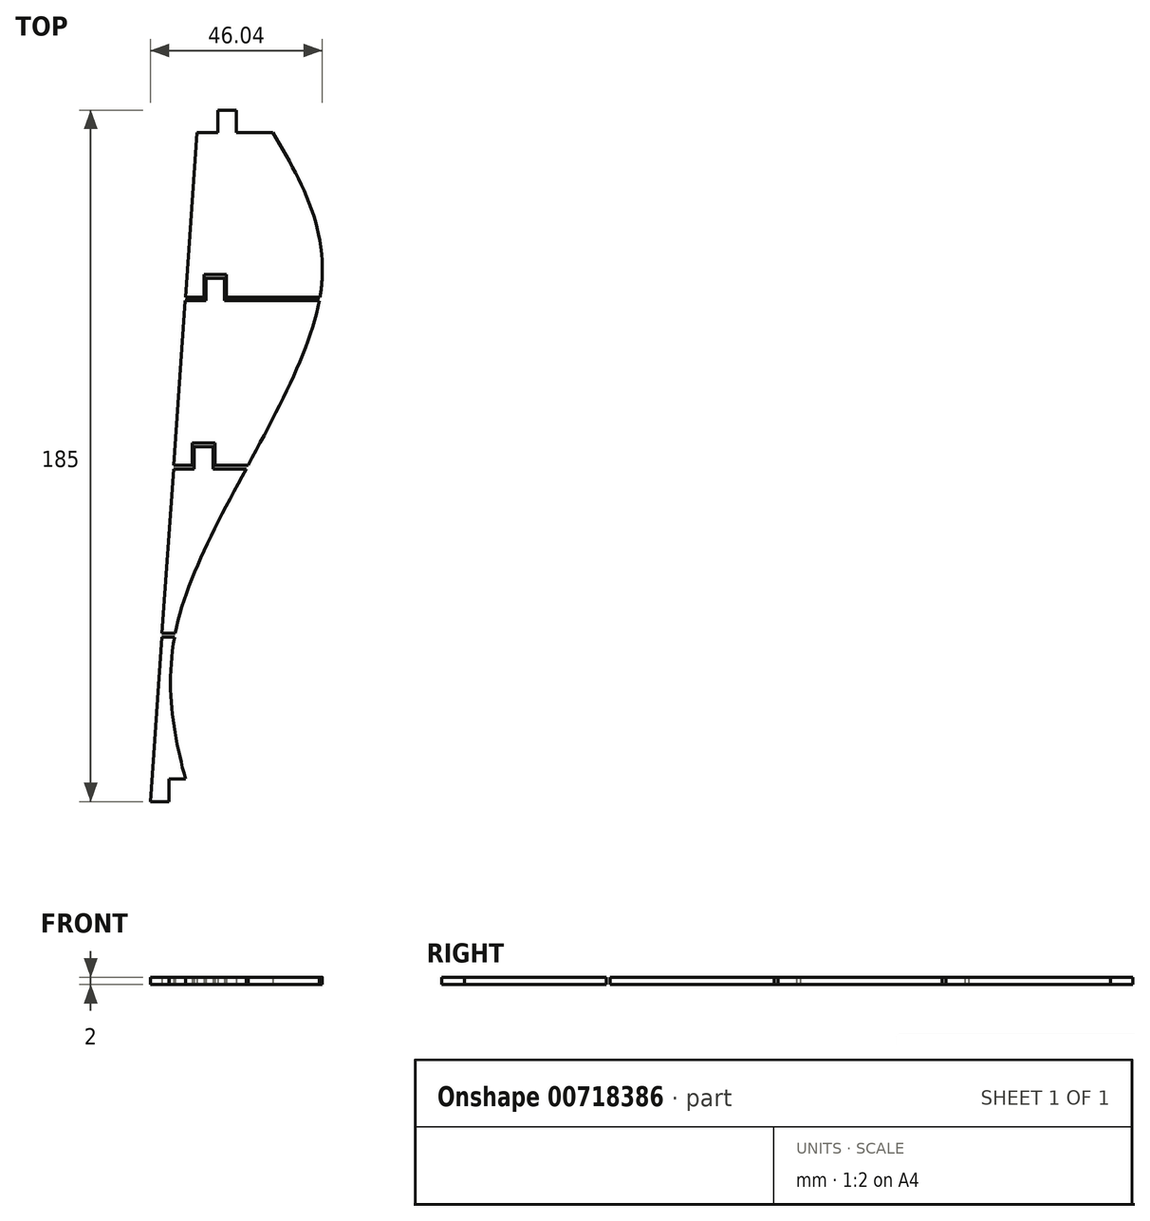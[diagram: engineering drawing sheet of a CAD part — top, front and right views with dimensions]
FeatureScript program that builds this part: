
annotation { "Feature Type Name" : "Feature", "Feature Type Description" : "" }
export const myFeature = defineFeature(function(context is Context, id is Id, definition is map)
    precondition{}
    {
        {
            var Q0;
            Q0=qCreatedBy(makeId("Top.planeOp"),FACE);
            var sketch = newSketch(context, id + "F0", { "sketchPlane" : qUnion([Q0])});
            skLineSegment(sketch, "E0", {"start": v(-23.52, 43.1) * mm, "end": v(-18.52, 43.1) * mm});
            skLineSegment(sketch, "E1", {"start": v(-26.65, -1.9) * mm, "end": v(-21.65, -1.9) * mm});
            skLineSegment(sketch, "E2", {"start": v(-29.78, -46.9) * mm, "end": v(-26.24, -46.9) * mm});
            skLineSegment(sketch, "E3", {"start": v(-32.9, -91.9) * mm, "end": v(-27.9, -91.9) * mm});
            skLineSegment(sketch, "E4.top", {"start": v(-18.52, 49.1) * mm, "end": v(-12.52, 49.1) * mm});
            skLineSegment(sketch, "E4.left", {"start": v(-18.52, 43.1) * mm, "end": v(-18.52, 49.1) * mm});
            skLineSegment(sketch, "E4.right", {"start": v(-12.52, 43.1) * mm, "end": v(-12.52, 49.1) * mm});
            skLineSegment(sketch, "E5.top", {"start": v(-21.65, 4.1) * mm, "end": v(-15.65, 4.1) * mm});
            skLineSegment(sketch, "E5.left", {"start": v(-21.65, -1.9) * mm, "end": v(-21.65, 4.1) * mm});
            skLineSegment(sketch, "E5.right", {"start": v(-15.65, -1.9) * mm, "end": v(-15.65, 4.1) * mm});
            skLineSegment(sketch, "E6.top", {"start": v(-27.9, -85.9) * mm, "end": v(-23.51, -85.9) * mm});
            skLineSegment(sketch, "E6.left", {"start": v(-27.9, -91.9) * mm, "end": v(-27.9, -85.9) * mm});
            skLineSegment(sketch, "E7.MirrorCS", {"start": v(12.52, 43.1) * mm, "end": v(12.52, 49.1) * mm});
            skLineSegment(sketch, "E8.MirrorCS", {"start": v(13.12, 49.1) * mm, "end": v(12.52, 49.1) * mm});
            skLineSegment(sketch, "E9", {"start": v(-20.46, 87.1) * mm, "end": v(-14.89, 87.1) * mm});
            skLineSegment(sketch, "E10", {"start": v(-23.59, 42.1) * mm, "end": v(-18.02, 42.1) * mm});
            skLineSegment(sketch, "E11", {"start": v(-26.72, -2.9) * mm, "end": v(-21.15, -2.9) * mm});
            skLineSegment(sketch, "E12", {"start": v(-29.84, -47.9) * mm, "end": v(-26.43, -47.9) * mm});
            skLineSegment(sketch, "E13.top", {"start": v(-14.89, 93.1) * mm, "end": v(-9.89, 93.1) * mm});
            skLineSegment(sketch, "E13.left", {"start": v(-14.89, 87.1) * mm, "end": v(-14.89, 93.1) * mm});
            skLineSegment(sketch, "E13.right", {"start": v(-9.89, 87.1) * mm, "end": v(-9.89, 93.1) * mm});
            skLineSegment(sketch, "E14.top", {"start": v(-18.02, 48.1) * mm, "end": v(-13.02, 48.1) * mm});
            skLineSegment(sketch, "E14.left", {"start": v(-18.02, 42.1) * mm, "end": v(-18.02, 48.1) * mm});
            skLineSegment(sketch, "E14.right", {"start": v(-13.02, 42.1) * mm, "end": v(-13.02, 48.1) * mm});
            skLineSegment(sketch, "E15.top", {"start": v(-21.15, 3.1) * mm, "end": v(-16.15, 3.1) * mm});
            skLineSegment(sketch, "E15.left", {"start": v(-21.15, -2.9) * mm, "end": v(-21.15, 3.1) * mm});
            skLineSegment(sketch, "E15.right", {"start": v(-16.15, -2.9) * mm, "end": v(-16.15, 3.1) * mm});
            skLineSegment(sketch, "E16.trimOffspring", {"start": v(-20.46, 87.1) * mm, "end": v(-23.52, 43.1) * mm});
            skLineSegment(sketch, "E17.trimOffspring", {"start": v(-9.89, 87.1) * mm, "end": v(-0.07, 87.1) * mm});
            skLineSegment(sketch, "E18.trimOffspring", {"start": v(-23.59, 42.1) * mm, "end": v(-26.65, -1.9) * mm});
            skLineSegment(sketch, "E19.trimOffspring", {"start": v(-12.52, 43.1) * mm, "end": v(12.52, 43.1) * mm});
            skLineSegment(sketch, "E20.trimOffspring", {"start": v(-13.02, 42.1) * mm, "end": v(12.34, 42.1) * mm});
            skLineSegment(sketch, "E21.trimOffspring", {"start": v(-26.72, -2.9) * mm, "end": v(-29.78, -46.9) * mm});
            skLineSegment(sketch, "E22.trimOffspring", {"start": v(-15.65, -1.9) * mm, "end": v(-6.73, -1.9) * mm});
            skLineSegment(sketch, "E23.trimOffspring", {"start": v(-16.15, -2.9) * mm, "end": v(-7.27, -2.9) * mm});
            skLineSegment(sketch, "E24.trimOffspring", {"start": v(-29.84, -47.9) * mm, "end": v(-32.9, -91.9) * mm});
            skLineSegment(sketch, "E25", {"start": v(-20.46, 87.1) * mm, "end": v(-0.07, 87.1) * mm, "construction": true});
            skFitSpline(sketch, "E26", {"points": [v(-0.07, 87.1) * mm, v(12.52, 43.1) * mm, v(-24.78, -40.9) * mm, v(-21.9, -91.9) * mm], "startDerivative": vector(80.76, -138.38) * mm, "endDerivative": vector(42.18, -155.15) * mm});
            skSolve(sketch);
        }
        {
            var Q0;
            Q0 = qSketchRegion(id + "F0", true);
            extrude(context, id + "F1", {"entities" : qUnion([Q0]), "depth" : 2 * mm, "offsetDistance" : 25 * mm});
        }
    });
